# Revit family: 94000182
name_source: partatom
category: Equipamentos hidráulicos
revit_build: Autodesk Revit 2016 (Build: 20150220_1215(x64)
units: mm (PartAtom-declared; Revit-internal decimal feet)

## family parameters
Compartilhado = Não
Corte com vazios quando carregados = Não
Cota do conector redondo = Utilizar diâmetro
Hospedeiro = Face
Ponto de cálculo do ambiente = Não
Tipo de parte = Normal

## types (1)
- Quadrum Undermount c/ Acessorios - 94000182
    Código de montagem = 94000182
    Descrição = 94000182
    Dimensões (mm) = 685 x 485 x 203
    Elevação-padrão = 1219
    Espessura Bancada = 20  [stored 0.0656168 ft]
    Fabricante = Tramontina
    Modelo = 94000182
    Nicho de corte para Instalação = 658 x 458
    Posição lixeira - horizontal = 889
    URL = https://www.tramontina.com.br
    posição horizontal dosador = 160  [stored 0.524934 ft]
    posição lixeira vertical = 106
    posição vertical - dosador = 465  [stored 1.52559 ft]

note: [stored X ft] marks values corroborated as IEEE doubles in the binary element streams (Revit-internal decimal feet)
